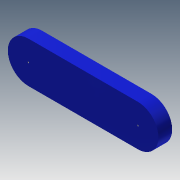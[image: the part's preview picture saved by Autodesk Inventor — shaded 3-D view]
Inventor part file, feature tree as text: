
AUTODESK INVENTOR PART (.ipt)
format: ipt  version: 2013 (Build 170138000, 138)  size: 98,816 bytes
history: native  units: mm
features: extrude x3, sketch x3
ambient origin geometry x8: Origin, YZ Plane, XZ Plane, XY Plane, X Axis, Y Axis, Z Axis, Center Point
bodies: Solid1 (feature_tree)
feature tree (6):
  extrude  "Extrusion1"  Depth=6.0mm
  extrude  "Extrusion2"  Depth=6.0mm
  extrude  "Extrusion3"  Depth=3.0mm
  sketch  "Sketch1"  dims[d0=16.0mm d1=6.0mm]
  sketch  "Sketch2"  dims[d2=6.0mm d3=6.0mm]
  sketch  "Sketch3"  dims[d4=2.0mm d5=0.0mm d6=3.0mm d7=3.0mm d8=2.0mm d9=0.0mm d10=0.2mm d11=0.2mm d12=2.0mm d13=0.0mm]
